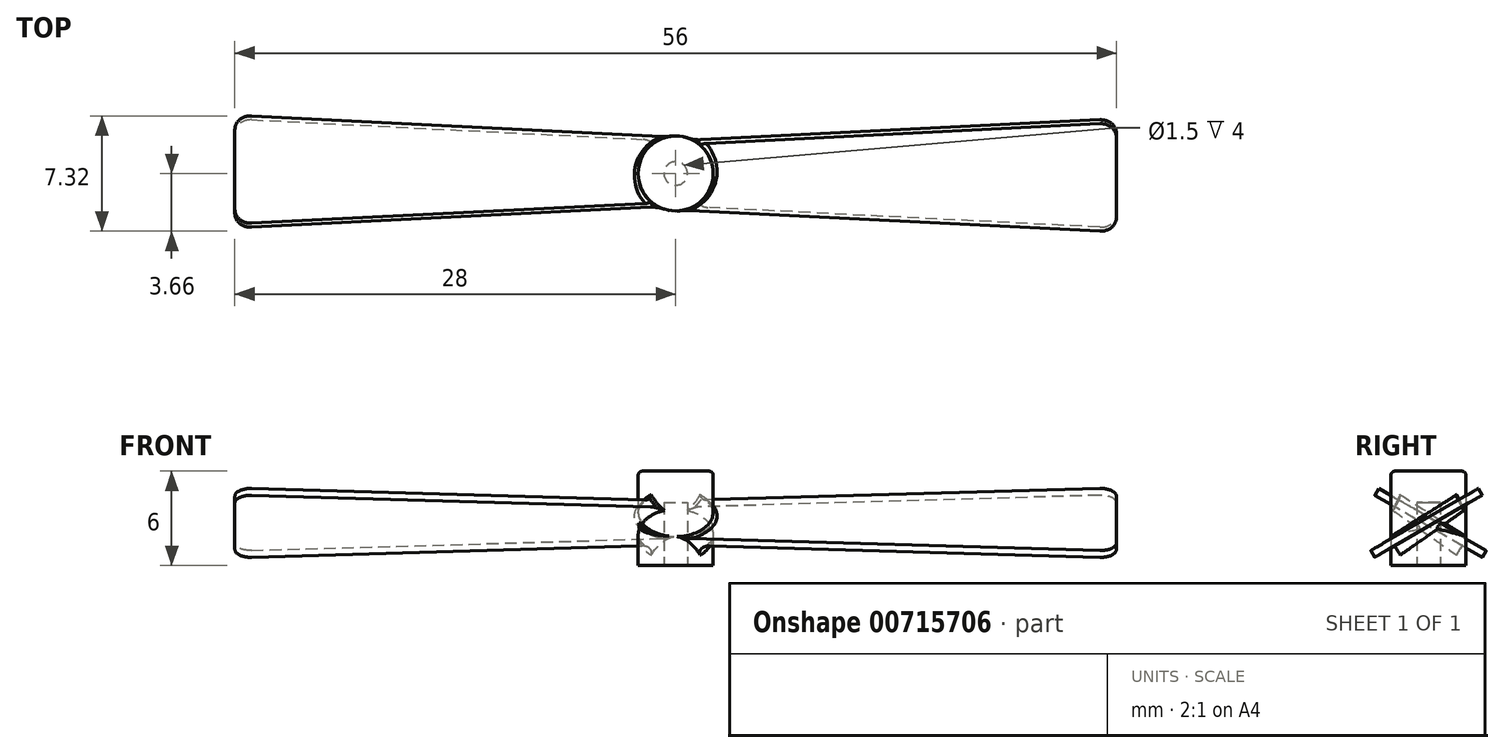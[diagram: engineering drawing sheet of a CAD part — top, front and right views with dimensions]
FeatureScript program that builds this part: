
annotation { "Feature Type Name" : "Feature", "Feature Type Description" : "" }
export const myFeature = defineFeature(function(context is Context, id is Id, definition is map)
    precondition{}
    {
        {
            var Q0;
            Q0=qCreatedBy(makeId("Top.planeOp"),FACE);
            var sketch = newSketch(context, id + "F0", { "sketchPlane" : qUnion([Q0])});
            skCircle(sketch, "E0", {"center": v(0, 0) * mm, "radius": 2.38 * mm});
            skLineSegment(sketch, "E1.right", {"start": v(-28, 4) * mm, "end": v(-28, -4) * mm});
            skLineSegment(sketch, "E2", {"start": v(0, 0) * mm, "end": v(-28, 0) * mm, "construction": true});
            skLineSegment(sketch, "E3", {"start": v(-28, -4) * mm, "end": v(0, -2.38) * mm});
            skLineSegment(sketch, "E4", {"start": v(-28, 4) * mm, "end": v(0, 2.38) * mm});
            skLineSegment(sketch, "E5", {"start": v(0, 2.38) * mm, "end": v(0, -2.38) * mm});
            skSolve(sketch);
        }
        {
            var Q0;
            Q0=makeQuery(id+"F0.imprint","IMPRINT",FACE,{"disambiguationData":[TD([[makeQuery(id+"F0.imprint","IMPRINT",EDGE,{"derivedFrom":sQuery(id+"F0.wireOp",EDGE,"E0")}),1.0]])]});
            extrude(context, id + "F1", {"entities" : qUnion([Q0]), "depth" : 6 * mm, "offsetDistance" : 25 * mm});
        }
        {
            var Q0;
            Q0=makeQuery(id+"F1.opExtrude","CAP_FACE",FACE,{"disambiguationData":[OSD([sQuery(id+"F0.wireOp",EDGE,"E0")])],"isStart":true});
            var sketch = newSketch(context, id + "F2", { "sketchPlane" : qUnion([Q0])});
            skCircle(sketch, "E6", {"center": v(0, 0) * mm, "radius": 0.75 * mm});
            skSolve(sketch);
        }
        {
            var Q0;
            Q0=makeQuery(id+"F0.imprint","IMPRINT",FACE,{"disambiguationData":[TD([[makeQuery(id+"F0.imprint","IMPRINT",EDGE,{"derivedFrom":sQuery(id+"F0.wireOp",EDGE,"E1.right")}),1.0]])]});
            var Q1;
            {var subQ0=sQuery(id+"F0.wireOp",EDGE,"E5");var subQ1=sQuery(id+"F0.wireOp",EDGE,"E0");var subQ2=makeQuery(id+"F0.imprint","INTERSECT",VERTEX,{"disambiguationData":[OD(0.0)],"derivedFrom":[subQ1,subQ0]});Q1=makeQuery(id+"F0.imprint","IMPRINT",FACE,{"disambiguationData":[TD([[makeQuery(id+"F0.imprint","IMPRINT",EDGE,{"disambiguationData":[TD([[subQ2,-1.0]])],"derivedFrom":subQ1}),1.0]])]});}
            extrude(context, id + "F3", {"entities" : qUnion([Q0, Q1]), "depth" : .5 * mm, "offsetDistance" : 25 * mm});
        }
        {
            var Q0;
            Q0=qCreatedBy(makeId("Right.planeOp"),FACE);
            var sketch = newSketch(context, id + "F4", { "sketchPlane" : qUnion([Q0])});
            skLineSegment(sketch, "E7", {"start": v(0, 0) * mm, "end": v(0, 7.4) * mm, "construction": true});
            skSolve(sketch);
        }
        {
            var Q0;
            Q0=makeQuery(id+"F3.opExtrude","SWEPT_BODY",BODY,{"disambiguationData":[OSD([sQuery(id+"F0.wireOp",EDGE,"E1.bottom"),sQuery(id+"F0.wireOp",EDGE,"E1.top"),sQuery(id+"F0.wireOp",EDGE,"E1.left"),sQuery(id+"F0.wireOp",EDGE,"E1.right")])]});
            var Q1;
            Q1=sQuery(id+"F0.wireOp",EDGE,"E2");
            transform(context, id + "F5", {"entities" : qUnion([Q0]), "transformType" : TransformType.ROTATION, "transformAxis" : qUnion([Q1]), "angle" : 30 * degree, "makeCopy" : false});
        }
        {
            var Q0;
            Q0=makeQuery(id+"F3.opExtrude","SWEPT_BODY",BODY,{"disambiguationData":[OSD([sQuery(id+"F0.wireOp",EDGE,"E1.bottom"),sQuery(id+"F0.wireOp",EDGE,"E1.top"),sQuery(id+"F0.wireOp",EDGE,"E1.left"),sQuery(id+"F0.wireOp",EDGE,"E1.right")])]});
            transform(context, id + "F6", {"entities" : qUnion([Q0]), "transformType" : TransformType.TRANSLATION_3D, "dx" : 0 * mm, "dy" : 0 * mm, "dz" : 2.5 * mm, "makeCopy" : false});
        }
        {
            var Q0;
            Q0=makeQuery(id+"F3.opExtrude","SWEPT_EDGE",EDGE,{"disambiguationData":[OSD([sQuery(id+"F0.wireOp",EDGE,"E1.top"),sQuery(id+"F0.wireOp",EDGE,"E1.right")])]});
            var Q1;
            Q1=makeQuery(id+"F3.opExtrude","SWEPT_EDGE",EDGE,{"disambiguationData":[OSD([sQuery(id+"F0.wireOp",EDGE,"E1.bottom"),sQuery(id+"F0.wireOp",EDGE,"E1.right")])]});
            fillet(context, id + "F7", {"entities" : qUnion([Q0, Q1]), "radius" : 1 * mm, "tangentPropagation" : true, "allowEdgeOverflow" : false});
        }
        {
            var Q0;
            Q0=makeQuery(id+"F3.opExtrude","SWEPT_BODY",BODY,{"disambiguationData":[OSD([sQuery(id+"F0.wireOp",EDGE,"E0"),sQuery(id+"F0.wireOp",EDGE,"E1.right"),sQuery(id+"F0.wireOp",EDGE,"E3"),sQuery(id+"F0.wireOp",EDGE,"E4"),sQuery(id+"F0.wireOp",EDGE,"E5")])]});
            var Q1;
            Q1=sQuery(id+"F4.wireOp",EDGE,"E7");
            circularPattern(context, id + "F8", {"entities" : qUnion([Q0]), "axis" : qUnion([Q1]), "angle" : 360 * degree, "instanceCount" : 2, "equalSpace" : true});
        }
        {
            var Q0;
            Q0=makeQuery(id+"F1.opExtrude","CAP_EDGE",EDGE,{"disambiguationData":[OSD([sQuery(id+"F0.wireOp",EDGE,"E0")])],"isStart":false});
            fillet(context, id + "F9", {"entities" : qUnion([Q0]), "radius" : .25 * mm, "tangentPropagation" : true, "allowEdgeOverflow" : false});
        }
        {
            var Q0;
            Q0=makeQuery(id+"F1.opExtrude","SWEPT_BODY",BODY,{"disambiguationData":[OSD([sQuery(id+"F0.wireOp",EDGE,"E0")])]});
            var Q1;
            Q1=makeQuery(id+"F3.opExtrude","SWEPT_BODY",BODY,{"disambiguationData":[OSD([sQuery(id+"F0.wireOp",EDGE,"E1.right"),sQuery(id+"F0.wireOp",EDGE,"E3"),sQuery(id+"F0.wireOp",EDGE,"E4"),sQuery(id+"F0.wireOp",EDGE,"E5")])]});
            var Q2;
            Q2=makeQuery(id+"F8.opPattern","COPY",BODY,{"derivedFrom":makeQuery(id+"F3.opExtrude","SWEPT_BODY",BODY,{"disambiguationData":[OSD([sQuery(id+"F0.wireOp",EDGE,"E1.right"),sQuery(id+"F0.wireOp",EDGE,"E3"),sQuery(id+"F0.wireOp",EDGE,"E4"),sQuery(id+"F0.wireOp",EDGE,"E5")])]}),"instanceName":"1"});
            booleanBodies(context, id + "F10", {"operationType" : BooleanOperationType.UNION, "tools" : qUnion([Q0, Q1, Q2])});
        }
        {
            var Q0;
            Q0 = qSketchRegion(id + "F2", true);
            extrude(context, id + "F11", {"entities" : qUnion([Q0]), "operationType" : NewBodyOperationType.REMOVE, "oppositeDirection" : true, "depth" : 4 * mm, "offsetDistance" : 25 * mm});
        }
        {
            var Q0;
            Q0=makeQuery(id+"F10.opBoolean","INTERSECT",EDGE,{"derivedFrom":[makeQuery(id+"F8.opPattern","COPY",FACE,{"derivedFrom":makeQuery(id+"F3.opExtrude","CAP_FACE",FACE,{"disambiguationData":[OSD([sQuery(id+"F0.wireOp",EDGE,"E1.right"),sQuery(id+"F0.wireOp",EDGE,"E3"),sQuery(id+"F0.wireOp",EDGE,"E4"),sQuery(id+"F0.wireOp",EDGE,"E5")])],"isStart":true}),"instanceName":"1"}),makeQuery(id+"F1.opExtrude","SWEPT_FACE",FACE,{"disambiguationData":[OSD([sQuery(id+"F0.wireOp",EDGE,"E0")])]})]});
            var Q1;
            Q1=makeQuery(id+"F10.opBoolean","INTERSECT",EDGE,{"derivedFrom":[makeQuery(id+"F3.opExtrude","CAP_FACE",FACE,{"disambiguationData":[OSD([sQuery(id+"F0.wireOp",EDGE,"E1.right"),sQuery(id+"F0.wireOp",EDGE,"E3"),sQuery(id+"F0.wireOp",EDGE,"E4"),sQuery(id+"F0.wireOp",EDGE,"E5")])],"isStart":true}),makeQuery(id+"F1.opExtrude","SWEPT_FACE",FACE,{"disambiguationData":[OSD([sQuery(id+"F0.wireOp",EDGE,"E0")])]})]});
            fillet(context, id + "F12", {"entities" : qUnion([Q0, Q1]), "radius" : .5 * mm, "allowEdgeOverflow" : false});
        }
        {
            var Q0;
            Q0=makeQuery(id+"F10.opBoolean","INTERSECT",EDGE,{"derivedFrom":[makeQuery(id+"F8.opPattern","COPY",FACE,{"derivedFrom":makeQuery(id+"F3.opExtrude","CAP_FACE",FACE,{"disambiguationData":[OSD([sQuery(id+"F0.wireOp",EDGE,"E1.right"),sQuery(id+"F0.wireOp",EDGE,"E3"),sQuery(id+"F0.wireOp",EDGE,"E4"),sQuery(id+"F0.wireOp",EDGE,"E5")])],"isStart":false}),"instanceName":"1"}),makeQuery(id+"F1.opExtrude","SWEPT_FACE",FACE,{"disambiguationData":[OSD([sQuery(id+"F0.wireOp",EDGE,"E0")])]})]});
            var Q1;
            Q1=makeQuery(id+"F10.opBoolean","INTERSECT",EDGE,{"derivedFrom":[makeQuery(id+"F3.opExtrude","CAP_FACE",FACE,{"disambiguationData":[OSD([sQuery(id+"F0.wireOp",EDGE,"E1.right"),sQuery(id+"F0.wireOp",EDGE,"E3"),sQuery(id+"F0.wireOp",EDGE,"E4"),sQuery(id+"F0.wireOp",EDGE,"E5")])],"isStart":false}),makeQuery(id+"F1.opExtrude","SWEPT_FACE",FACE,{"disambiguationData":[OSD([sQuery(id+"F0.wireOp",EDGE,"E0")])]})]});
            fillet(context, id + "F13", {"entities" : qUnion([Q0, Q1]), "radius" : .25 * mm, "allowEdgeOverflow" : false});
        }
        {
            var Q0;
            Q0=makeQuery(id+"F10.opBoolean","INTERSECT",EDGE,{"derivedFrom":[makeQuery(id+"F3.opExtrude","SWEPT_FACE",FACE,{"disambiguationData":[OSD([sQuery(id+"F0.wireOp",EDGE,"E3")])]}),makeQuery(id+"F1.opExtrude","SWEPT_FACE",FACE,{"disambiguationData":[OSD([sQuery(id+"F0.wireOp",EDGE,"E0")])]})]});
            var Q1;
            Q1=makeQuery(id+"F10.opBoolean","INTERSECT",EDGE,{"derivedFrom":[makeQuery(id+"F8.opPattern","COPY",FACE,{"derivedFrom":makeQuery(id+"F3.opExtrude","SWEPT_FACE",FACE,{"disambiguationData":[OSD([sQuery(id+"F0.wireOp",EDGE,"E3")])]}),"instanceName":"1"}),makeQuery(id+"F1.opExtrude","SWEPT_FACE",FACE,{"disambiguationData":[OSD([sQuery(id+"F0.wireOp",EDGE,"E0")])]})]});
            fillet(context, id + "F14", {"entities" : qUnion([Q0, Q1]), "radius" : .25 * mm, "allowEdgeOverflow" : false});
        }
    });
